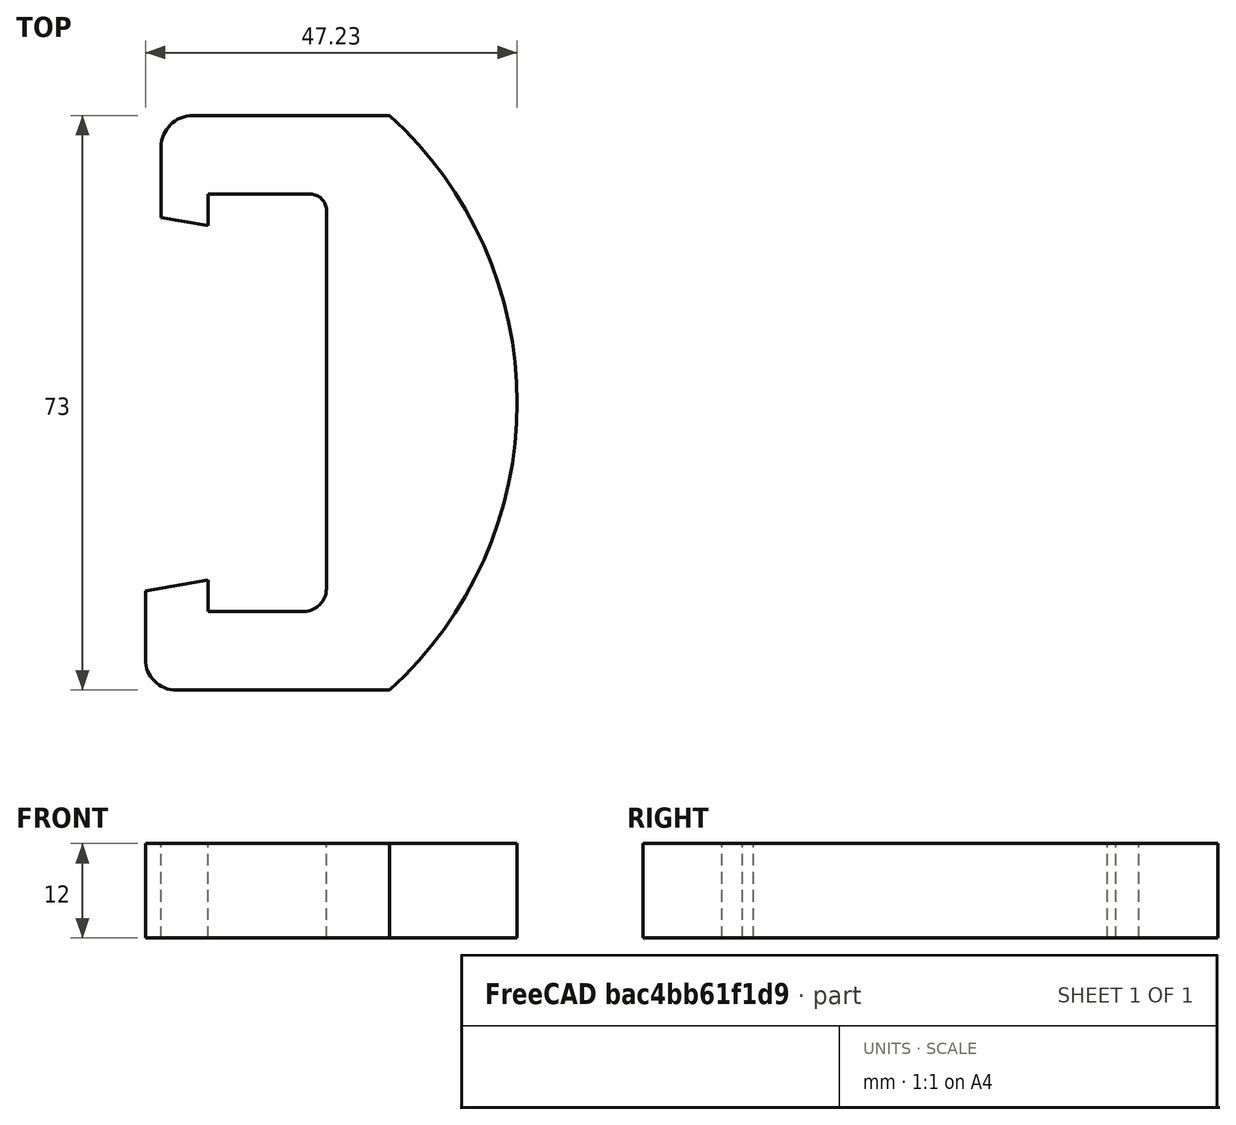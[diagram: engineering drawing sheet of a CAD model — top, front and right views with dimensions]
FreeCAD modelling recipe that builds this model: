
FCSTD DOCUMENT  (FreeCAD 0.16R)
Label: RaftyClip
License: All rights reserved
LicenseURL: http://en.wikipedia.org/wiki/All_rights_reserved
objects: Sketcher::SketchObject×1, PartDesign::Pad×1, Mesh::Feature×1
note: 3 computed .brp shape members not serialized (recipe doc carries the construction recipe); baked Part::Feature solids carry a one-line shape summary decoded from their .brp

FEATURE [Sketcher::SketchObject] Sketch
  sketch-geometry (16):
    g0: LineSegment StartX=-6 StartY=23.558 StartZ=0 EndX=-6 EndY=32.4656 EndZ=0
    g1: LineSegment StartX=-1.96561 StartY=36.5 StartZ=0 EndX=23.0344 EndY=36.5 EndZ=0
    g2: LineSegment StartX=23.0344 StartY=-36.5 StartZ=0 EndX=-4.08896 EndY=-36.5 EndZ=0
    g3: LineSegment StartX=-8 StartY=-32.589 StartZ=0 EndX=-8 EndY=-23.9106 EndZ=0
    g4: LineSegment StartX=-8 StartY=-23.9106 StartZ=0 EndX=0 EndY=-22.5 EndZ=0
    g5: LineSegment StartX=0 StartY=-22.5 StartZ=0 EndX=0 EndY=-26.5 EndZ=0
    g6: LineSegment StartX=0 StartY=-26.5 StartZ=0 EndX=12.1251 EndY=-26.5 EndZ=0
    g7: LineSegment StartX=14.9977 StartY=-23.6275 StartZ=0 EndX=14.9977 EndY=24.4659 EndZ=0
    g8: LineSegment StartX=12.9635 StartY=26.5 StartZ=0 EndX=0 EndY=26.5 EndZ=0
    g9: LineSegment StartX=0 StartY=26.5 StartZ=0 EndX=0 EndY=22.5 EndZ=0
    g10: LineSegment StartX=0 StartY=22.5 StartZ=0 EndX=-6 EndY=23.558 EndZ=0
    g11: ArcOfCircle CenterX=12.9635 CenterY=24.4659 CenterZ=0 NormalX=0 NormalY=0 NormalZ=1 Radius=2.03413 StartAngle=0 EndAngle=1.5708
    g12: ArcOfCircle CenterX=12.1251 CenterY=-23.6275 CenterZ=0 NormalX=0 NormalY=0 NormalZ=1 Radius=2.87252 StartAngle=4.71239 EndAngle=6.28319
    g13: ArcOfCircle CenterX=-1.96561 CenterY=32.4656 CenterZ=0 NormalX=0 NormalY=0 NormalZ=1 Radius=4.03439 StartAngle=1.5708 EndAngle=3.14159
    g14: ArcOfCircle CenterX=-4.08896 CenterY=-32.589 CenterZ=0 NormalX=0 NormalY=0 NormalZ=1 Radius=3.91104 StartAngle=3.14159 EndAngle=4.71239
    g15: ArcOfCircle CenterX=-10 CenterY=0 CenterZ=0 NormalX=0 NormalY=0 NormalZ=1 Radius=49.2293 StartAngle=5.44799 EndAngle=7.11838
  constraints (40):
    c: Vertical(g0)
    c: Horizontal(g2)
    c: Coincident(g3,g4)
    c: Coincident(g4,g5)
    c: Coincident(g5,g6)
    c: Horizontal(g6)
    c: Vertical(g7)
    c: Horizontal(g8)
    c: Coincident(g8,g9)
    c: Vertical(g9)
    c: Coincident(g9,g10)
    c: Coincident(g10,g0)
    c: PointOnObject(g8,g-2)
    c: Vertical(g3)
    c: PointOnObject(g4,g-2)
    c: Vertical(g5)
    c: DistanceX(g0) = -6
    c: Angle(g10) = 2.96706
    c: Horizontal(g1)
    c: DistanceX(g3) = -8
    c: Angle(g4) = 0.174533
    c: Distance(g5) = 4
    c: Distance(g9) = 4
    c: Distance(g8,g1) = 10
    c: Distance(g4,g9) = 45
    c: Distance(g5,g2) = 10
    c: Symmetric(g9,g4,g-1)
    c: Tangent(g8,g11) = -1.5708
    c: Tangent(g7,g11) = -1.5708
    c: Tangent(g6,g12) = -1.5708
    c: Tangent(g7,g12) = -1.5708
    c: Tangent(g1,g13) = 1.5708
    c: Tangent(g0,g13) = 1.5708
    c: Tangent(g2,g14) = 1.5708
    c: Tangent(g3,g14) = 1.5708
    c: Coincident(g15,g2)
    c: Coincident(g15,g1)
    c: PointOnObject(g15,g-1)
    c: DistanceX(g15) = -10
    c: Distance(g1) = 25
FEATURE [PartDesign::Pad] Pad
  Length = 12
  Length2 = 100
  Sketch = -> Sketch
  Type = 0
FEATURE [Mesh::Feature] Mesh  label="Pad (Meshed)"
